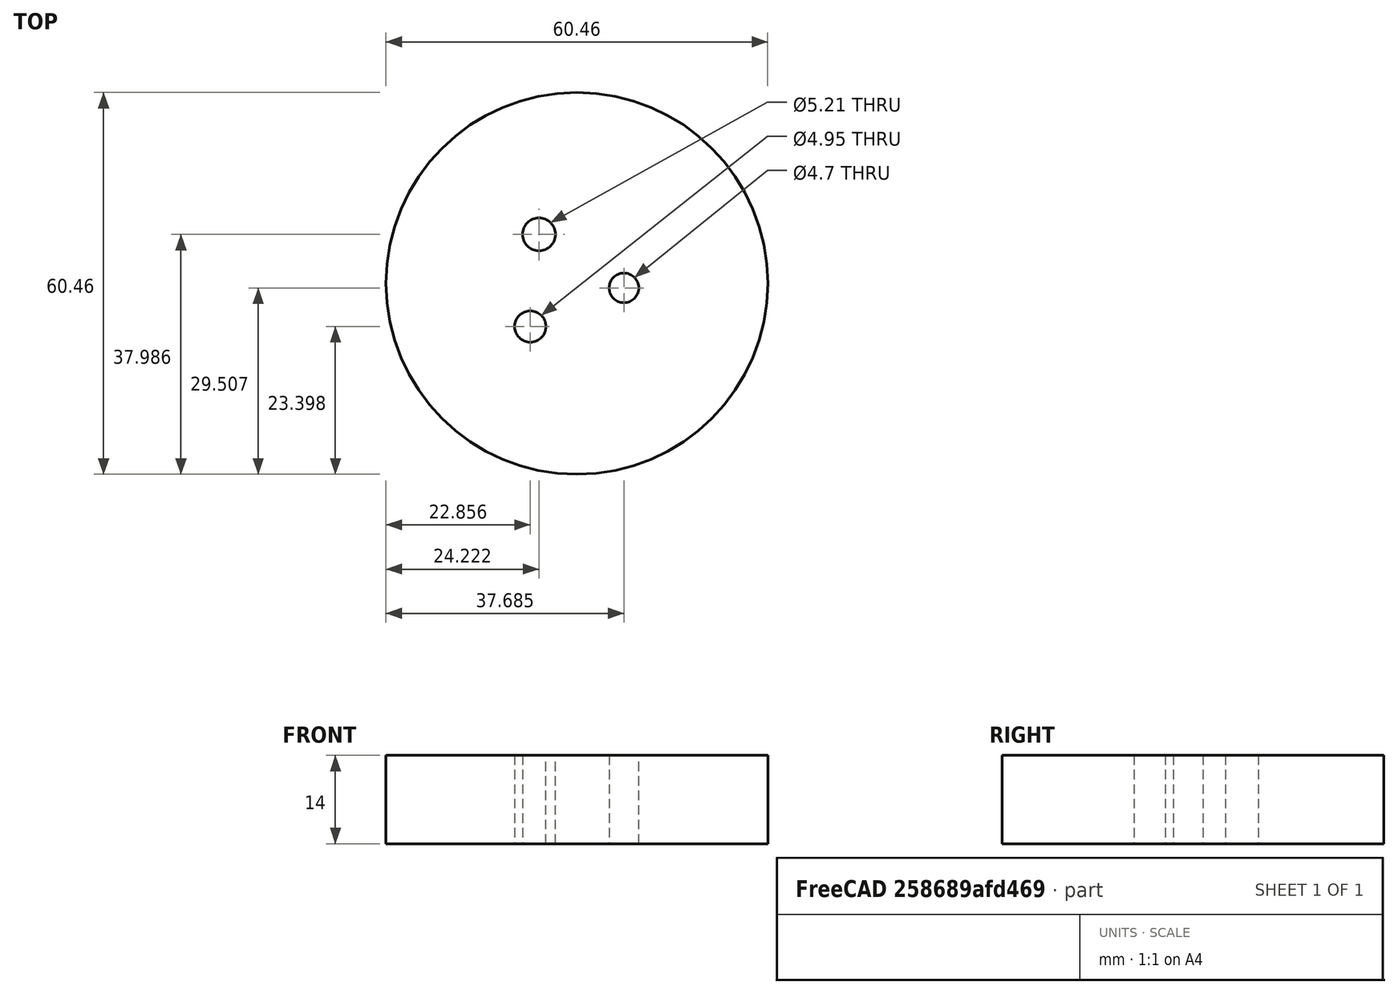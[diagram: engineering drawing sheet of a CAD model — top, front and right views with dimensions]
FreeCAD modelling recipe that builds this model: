
FCSTD DOCUMENT  (FreeCAD 0.18R14778 (Git))
Label: sketchexport_shapebinder
License: All rights reserved
LicenseURL: http://en.wikipedia.org/wiki/All_rights_reserved
objects: Sketcher::SketchObject×2, PartDesign::Pad×2, PartDesign::Body×2, PartDesign::SubShapeBinder×1, Sketcher::SketchExport×1
note: 10 computed .brp shape members not serialized (recipe doc carries the construction recipe); baked Part::Feature solids carry a one-line shape summary decoded from their .brp

FEATURE [Sketcher::SketchObject] Sketch
  LastGeoID = 4
  MapMode = 5
  Support = -> [XY_Plane]
  sketch-geometry (4):
    g0: Circle CenterX=0 CenterY=0 CenterZ=0 NormalX=0 NormalY=0 NormalZ=1 AngleXU=0 Radius=30.2328
    g1: Circle CenterX=-7.37428 CenterY=-6.83176 CenterZ=0 NormalX=0 NormalY=0 NormalZ=1 AngleXU=0 Radius=2.47589
    g2: Circle CenterX=-6.00793 CenterY=7.75605 CenterZ=0 NormalX=0 NormalY=0 NormalZ=1 AngleXU=0 Radius=2.60364
    g3: Circle CenterX=7.45465 CenterY=-0.723363 CenterZ=0 NormalX=0 NormalY=0 NormalZ=1 AngleXU=0 Radius=2.35163
  constraints (1):
    c: Coincident(g0,g-1)
FEATURE [PartDesign::Pad] Pad
  ClaimChildren = false
  Length = 14
  Length2 = 100
  Profile = -> Sketch
  Type = 0
FEATURE [PartDesign::Body] Body  label="base"
  Group = -> [Sketch,Pad]
  Origin = -> Origin
  Tip = -> Pad
FEATURE [PartDesign::SubShapeBinder] Binder
  BindMode = 0
  ClaimChildren = false
  Fuse = true
  MakeFace = true
  PartialLoad = true
  Placement = pos=(0,0,-14) rot=(0,0,1;0rad)
  Relative = true
  Support = -> Body
FEATURE [Sketcher::SketchExport] Export
  Base = Sketch001
  Refs = ;e116.ExternalEdge1 | ;e117.ExternalEdge3 | ;e118.ExternalEdge2 | ;e119.ExternalEdge4
  SyncPlacement = true
FEATURE [Sketcher::SketchObject] Sketch001
  Exports = -> [Export]
  ExternalGeometry = -> [Binder]
  LastGeoID = 0
  MapMode = 5
  Support = -> [Binder]
FEATURE [PartDesign::Pad] Pad001
  ClaimChildren = false
  Length = 10
  Length2 = 100
  Profile = -> Export
  Type = 0
FEATURE [PartDesign::Body] Body001  label="hat"
  Group = -> [Binder,Sketch001,Export,Pad001]
  Origin = -> Origin001
  Placement = pos=(0,0,14) rot=(0,0,1;0rad)
  Tip = -> Pad001
